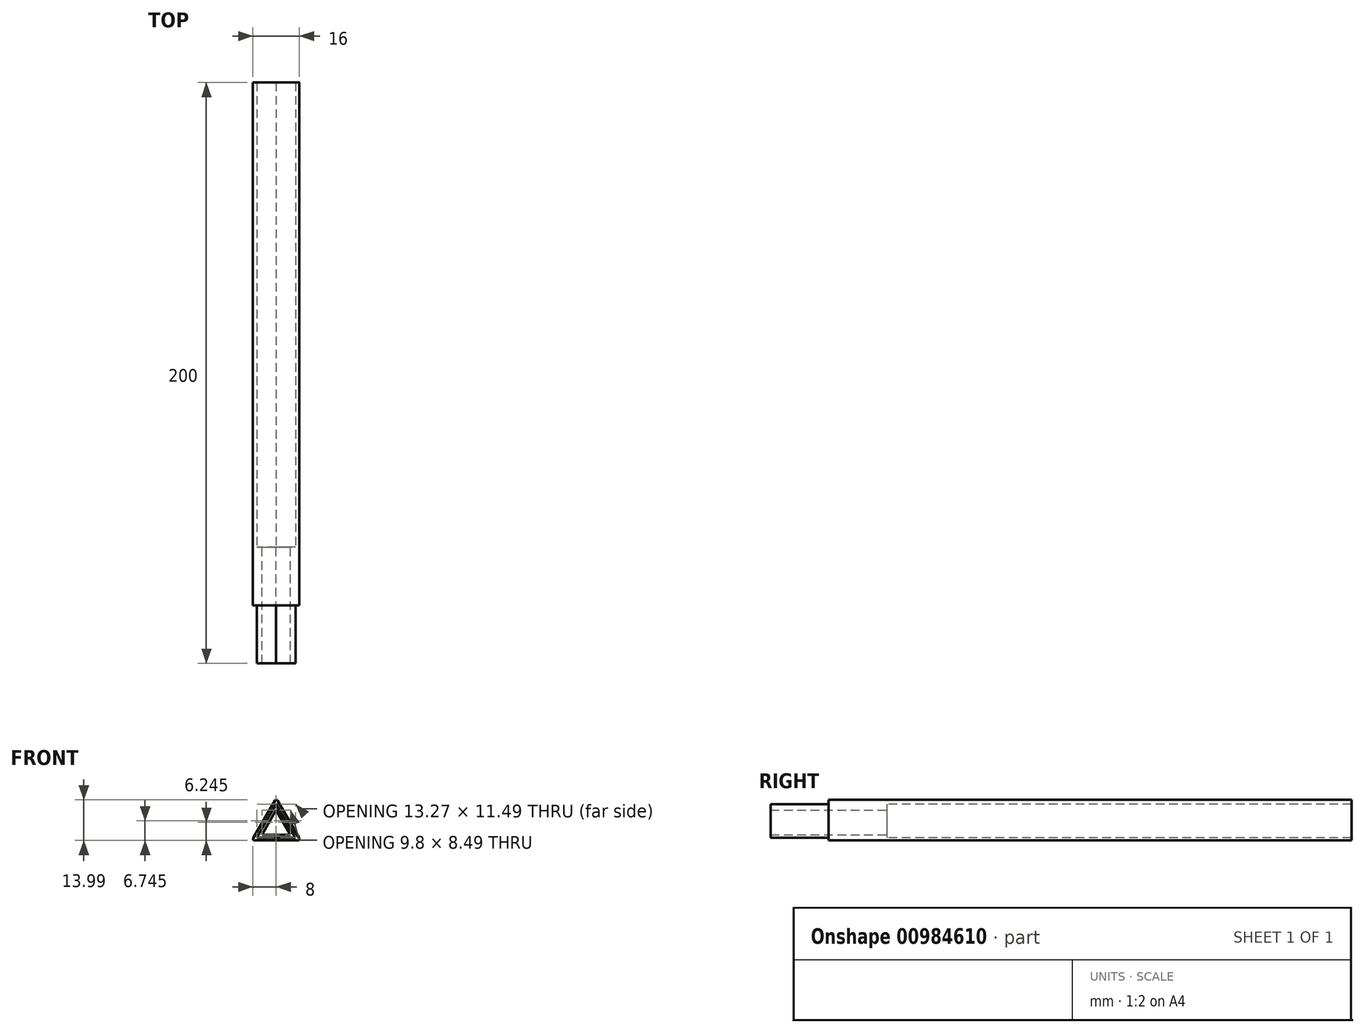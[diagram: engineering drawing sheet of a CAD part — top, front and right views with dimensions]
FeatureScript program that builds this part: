
annotation { "Feature Type Name" : "Feature", "Feature Type Description" : "" }
export const myFeature = defineFeature(function(context is Context, id is Id, definition is map)
    precondition{}
    {
        {
            var Q0;
            Q0=qCreatedBy(makeId("Front.planeOp"),FACE);
            var sketch = newSketch(context, id + "F0", { "sketchPlane" : qUnion([Q0])});
            skLineSegment(sketch, "E0", {"start": v(-7.5, 0) * mm, "end": v(7.5, 0) * mm});
            skLineSegment(sketch, "E1", {"start": v(7.93, 0.75) * mm, "end": v(0.43, 13.74) * mm});
            skLineSegment(sketch, "E2", {"start": v(-0.43, 13.74) * mm, "end": v(-7.93, 0.75) * mm});
            skLineSegment(sketch, "E3", {"start": v(0, 14.5) * mm, "end": v(0, 0) * mm, "construction": true});
            skPoint(sketch, "E4.visualSharp", {"position": v(0, 14.5) * mm});
            skArc(sketch, "E4.filletArc", {"start": v(0.43, 13.74) * mm, "mid": v(0, 14) * mm, "end": v(-0.43, 13.74) * mm});
            skPoint(sketch, "E5.visualSharp", {"position": v(8.37, 0) * mm});
            skArc(sketch, "E5.filletArc", {"start": v(7.5, 0) * mm, "mid": v(7.93, 0.25) * mm, "end": v(7.93, 0.75) * mm});
            skPoint(sketch, "E6.visualSharp", {"position": v(-8.37, 0) * mm});
            skArc(sketch, "E6.filletArc", {"start": v(-7.93, 0.75) * mm, "mid": v(-7.93, 0.25) * mm, "end": v(-7.5, 0) * mm});
            skLineSegment(sketch, "E7.0", {"start": v(0, 12.5) * mm, "end": v(-6.63, 1) * mm});
            skLineSegment(sketch, "E7.1", {"start": v(6.63, 1) * mm, "end": v(0, 12.5) * mm});
            skLineSegment(sketch, "E7.2", {"start": v(-6.63, 1) * mm, "end": v(6.63, 1) * mm});
            skLineSegment(sketch, "E8.0", {"start": v(0, 10.5) * mm, "end": v(-4.9, 2) * mm});
            skLineSegment(sketch, "E8.1", {"start": v(4.9, 2) * mm, "end": v(0, 10.5) * mm});
            skLineSegment(sketch, "E8.2", {"start": v(-4.9, 2) * mm, "end": v(4.9, 2) * mm});
            skLineSegment(sketch, "E9", {"start": v(4.9, 2) * mm, "end": v(0, 4.83) * mm, "construction": true});
            skLineSegment(sketch, "E10", {"start": v(0, 4.83) * mm, "end": v(-4.9, 2) * mm, "construction": true});
            skLineSegment(sketch, "E11", {"start": v(0, 4.83) * mm, "end": v(0, 10.5) * mm, "construction": true});
            skSolve(sketch);
        }
        {
            var Q0;
            Q0=makeQuery(id+"F0.imprint","IMPRINT",FACE,{"disambiguationData":[TD([[makeQuery(id+"F0.imprint","IMPRINT",EDGE,{"derivedFrom":sQuery(id+"F0.wireOp",EDGE,"E0")}),1.0]])]});
            extrude(context, id + "F1", {"entities" : qUnion([Q0]), "oppositeDirection" : true, "depth" : 180 * mm, "offsetDistance" : 25 * mm});
        }
        {
            var Q0;
            Q0=makeQuery(id+"F0.imprint","IMPRINT",FACE,{"disambiguationData":[TD([[makeQuery(id+"F0.imprint","IMPRINT",EDGE,{"derivedFrom":sQuery(id+"F0.wireOp",EDGE,"E7.0")}),1.0]])]});
            extrude(context, id + "F2", {"entities" : qUnion([Q0]), "operationType" : NewBodyOperationType.ADD, "depth" : 20 * mm, "offsetDistance" : 25 * mm, "hasSecondDirection" : true, "secondDirectionOppositeDirection" : true, "secondDirectionDepth" : 20 * mm});
        }
    });
